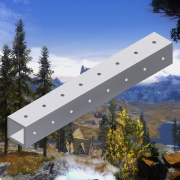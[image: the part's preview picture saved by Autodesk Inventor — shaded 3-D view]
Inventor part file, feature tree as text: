
AUTODESK INVENTOR PART (.ipt)
format: ipt  version: 2015 SP1 (Build 190203100, 203)  size: 190,464 bytes
history: native  units: in
note: dims shown in document units (in); Inventor stores cm internally (conversion verified against a paired STEP export)
features: sketch x3, hole x2, extrude x1
ambient origin geometry x8: Origin, YZ Plane, XZ Plane, XY Plane, X Axis, Y Axis, Z Axis, Center Point
bodies: Solid1 (feature_tree)
feature tree (6):
  extrude  "Extrusion1"  Depth=1.0in
  hole  "Hole2"  [1 undecoded]
  hole  "Hole3"  [1 undecoded]
  sketch  "Sketch1"  dims[d0=1.0in d1=1.0in]
  sketch  "Sketch6"  dims[d6=0.125in d7=0.125in]
  sketch  "Sketch7"  dims[d8=8.0in d9=0.0in d23=0.5in d24=0.5in d25=3.1496in d27=1.0in d28=0.3937in d30=1.0in d32=0.163in d33=0.75in d34=0.375in d35=0.25in d36=0.5635in d37=1.0in d38=0.8108in d39=0.5in d40=0.5in d41=3.1496in d43=1.0in d44=0.3937in d46=1.0in d48=0.163in d49=0.75in d50=0.375in d51=0.25in d52=0.5635in d53=1.0in d54=0.8108in]
note: 2 required parameter values undecoded (feature->parameter linkage not recoverable at this tier; creation-order binding heuristic only, values carry confidence <= 0.55)
